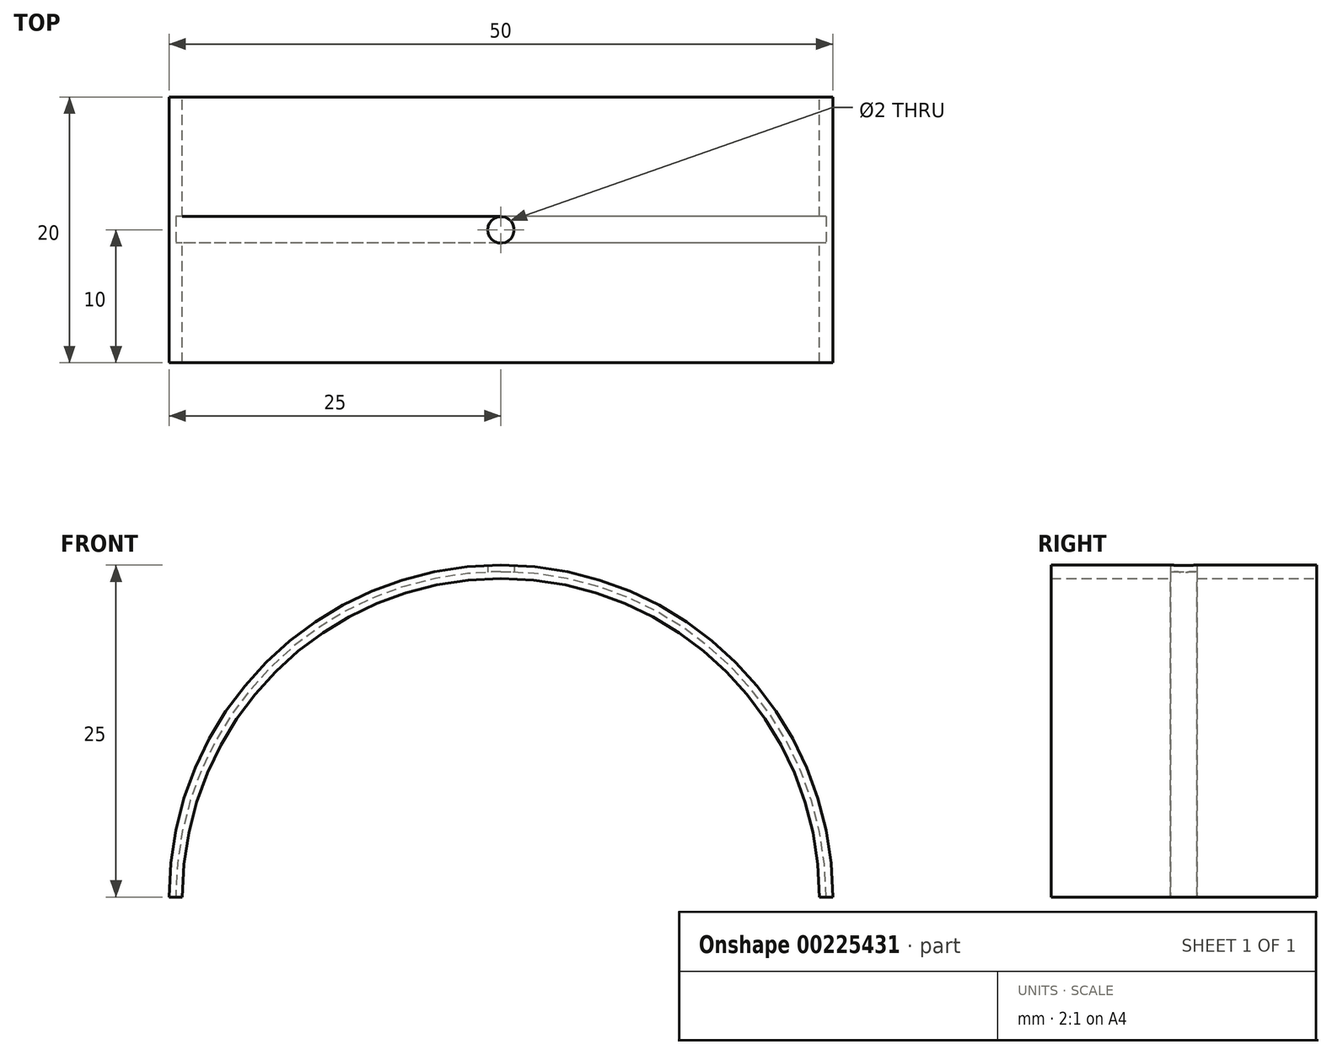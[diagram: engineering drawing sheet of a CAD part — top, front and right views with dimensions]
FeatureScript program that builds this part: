
annotation { "Feature Type Name" : "Feature", "Feature Type Description" : "" }
export const myFeature = defineFeature(function(context is Context, id is Id, definition is map)
    precondition{}
    {
        {
            var Q0;
            Q0=qCreatedBy(makeId("Front.planeOp"),FACE);
            var sketch = newSketch(context, id + "F0", { "sketchPlane" : qUnion([Q0])});
            skArc(sketch, "E0", {"start": v(25, 0) * mm, "mid": v(0, 25) * mm, "end": v(-25, 0) * mm});
            skArc(sketch, "E1.0", {"start": v(24, 0) * mm, "mid": v(0, 24) * mm, "end": v(-24, 0) * mm});
            skLineSegment(sketch, "E2", {"start": v(-25, 0) * mm, "end": v(-24, 0) * mm});
            skPoint(sketch, "E3.orphan", {"position": v(-27.21, 0) * mm});
            skLineSegment(sketch, "E4.trimOffspring", {"start": v(24, 0) * mm, "end": v(25, 0) * mm});
            skSolve(sketch);
        }
        {
            var Q0;
            Q0=qSketchRegion(id+"F0",true);
            extrude(context, id + "F1", {"entities" : qUnion([Q0]), "endBound" : BoundingType.SYMMETRIC, "depth" : 20 * mm});
        }
        {
            var Q0;
            Q0=qCreatedBy(makeId("Top.planeOp"),FACE);
            var sketch = newSketch(context, id + "F2", { "sketchPlane" : qUnion([Q0])});
            skLineSegment(sketch, "E5.bottom", {"start": v(-24.5, 1) * mm, "end": v(-24, 1) * mm});
            skLineSegment(sketch, "E5.top", {"start": v(-24.5, -1) * mm, "end": v(-24, -1) * mm});
            skLineSegment(sketch, "E5.left", {"start": v(-24.5, 1) * mm, "end": v(-24.5, -1) * mm});
            skLineSegment(sketch, "E5.right", {"start": v(-24, 1) * mm, "end": v(-24, -1) * mm});
            skPoint(sketch, "E5.middle", {"position": v(-24.25, 0) * mm});
            skSolve(sketch);
        }
        {
            var Q0;
            Q0=qSketchRegion(id+"F2",true);
            var Q1;
            Q1=makeQuery(id+"F1.opExtrude","SWEPT_FACE",FACE,{"disambiguationData":[OSD([sQuery(id+"F0.wireOp",EDGE,"E1.0")])]});
            revolve(context, id + "F3", {"operationType" : NewBodyOperationType.REMOVE, "entities" : qUnion([Q0]), "axis" : qUnion([Q1]), "revolveType" : RevolveType.FULL, "oppositeDirection" : true});
        }
        {
            var Q0;
            Q0=qCreatedBy(makeId("Top.planeOp"),FACE);
            var sketch = newSketch(context, id + "F4", { "sketchPlane" : qUnion([Q0])});
            skCircle(sketch, "E6", {"center": v(0, 0) * mm, "radius": 1 * mm});
            skSolve(sketch);
        }
        {
            var Q0;
            Q0=qSketchRegion(id+"F4",true);
            extrude(context, id + "F5", {"entities" : qUnion([Q0]), "operationType" : NewBodyOperationType.REMOVE, "endBound" : BoundingType.THROUGH_ALL, "depth" : 25 * mm});
        }
    });
